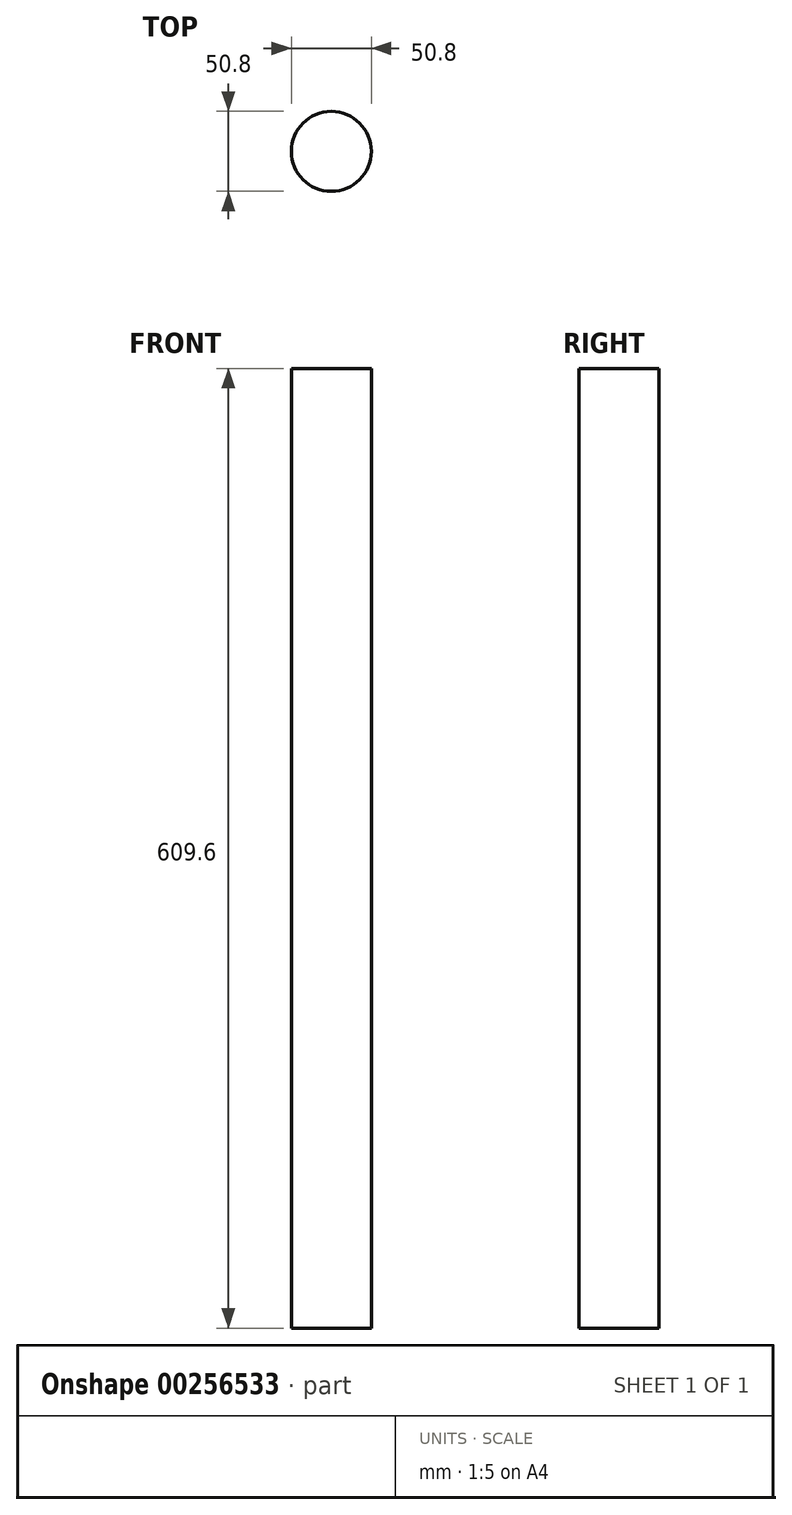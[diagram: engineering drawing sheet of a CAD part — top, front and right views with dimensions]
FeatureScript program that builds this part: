
annotation { "Feature Type Name" : "Feature", "Feature Type Description" : "" }
export const myFeature = defineFeature(function(context is Context, id is Id, definition is map)
    precondition{}
    {
        {
            var Q0;
            Q0=qCreatedBy(makeId("Top.planeOp"),FACE);
            var sketch = newSketch(context, id + "F0", { "sketchPlane" : qUnion([Q0])});
            skCircle(sketch, "E0", {"center": v(0, 0) * mm, "radius": 25.4 * mm});
            skSolve(sketch);
        }
        {
            var Q0;
            Q0 = qSketchRegion(id + "F0", true);
            extrude(context, id + "F1", {"entities" : qUnion([Q0]), "depth" : 609.6 * mm});
        }
    });
